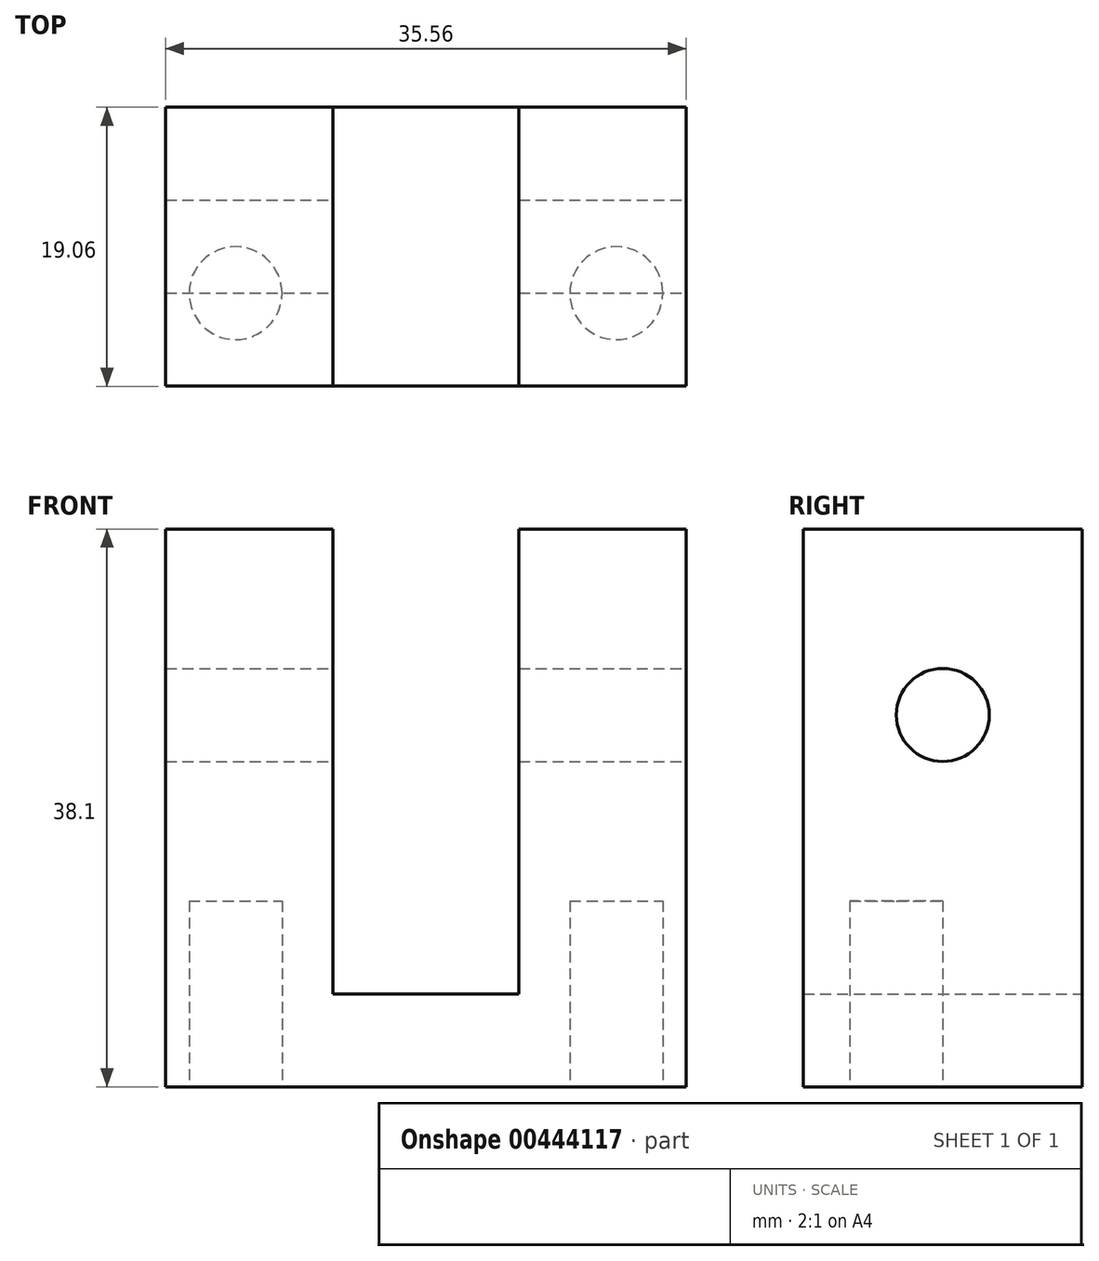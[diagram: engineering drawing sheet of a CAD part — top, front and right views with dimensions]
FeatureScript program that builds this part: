
annotation { "Feature Type Name" : "Feature", "Feature Type Description" : "" }
export const myFeature = defineFeature(function(context is Context, id is Id, definition is map)
    precondition{}
    {
        {
            var Q0;
            Q0=qCreatedBy(makeId("Front.planeOp"),FACE);
            var sketch = newSketch(context, id + "F0", { "sketchPlane" : qUnion([Q0])});
            skLineSegment(sketch, "E0", {"start": v(0, 0) * mm, "end": v(0, 38.1) * mm});
            skLineSegment(sketch, "E1", {"start": v(0, 38.1) * mm, "end": v(11.43, 38.1) * mm});
            skLineSegment(sketch, "E2", {"start": v(11.43, 38.1) * mm, "end": v(11.43, 6.35) * mm});
            skLineSegment(sketch, "E3", {"start": v(11.43, 6.35) * mm, "end": v(24.13, 6.35) * mm});
            skLineSegment(sketch, "E4", {"start": v(24.13, 6.35) * mm, "end": v(24.13, 38.1) * mm});
            skLineSegment(sketch, "E5", {"start": v(24.13, 38.1) * mm, "end": v(35.56, 38.1) * mm});
            skLineSegment(sketch, "E6", {"start": v(35.56, 38.1) * mm, "end": v(35.56, 0) * mm});
            skLineSegment(sketch, "E7", {"start": v(35.56, 0) * mm, "end": v(0, 0) * mm});
            skLineSegment(sketch, "E8", {"start": v(-7.8, 25.4) * mm, "end": v(70.8, 25.4) * mm, "construction": true});
            skSolve(sketch);
        }
        {
            var Q0;
            Q0 = qSketchRegion(id + "F0", true);
            extrude(context, id + "F1", {"entities" : qUnion([Q0]), "endBound" : BoundingType.SYMMETRIC, "depth" : 19.05 * mm});
        }
        {
            var Q0;
            Q0=makeQuery(id+"F1.opExtrude","SWEPT_FACE",FACE,{"disambiguationData":[OSD([sQuery(id+"F0.wireOp",EDGE,"E6")])]});
            var sketch = newSketch(context, id + "F2", { "sketchPlane" : qUnion([Q0])});
            skLineSegment(sketch, "E9", {"start": v(-10.35, 25.4) * mm, "end": v(27.89, 25.4) * mm, "construction": true});
            skCircle(sketch, "E10", {"center": v(0, 25.4) * mm, "radius": 3.18 * mm});
            skSolve(sketch);
        }
        {
            var Q0;
            Q0 = qSketchRegion(id + "F2", true);
            extrude(context, id + "F3", {"entities" : qUnion([Q0]), "operationType" : NewBodyOperationType.REMOVE, "endBound" : BoundingType.THROUGH_ALL, "oppositeDirection" : true, "depth" : 25.4 * mm});
        }
        {
            var Q0;
            Q0=makeQuery(id+"F1.opExtrude","SWEPT_FACE",FACE,{"disambiguationData":[OSD([sQuery(id+"F0.wireOp",EDGE,"E7")])]});
            var sketch = newSketch(context, id + "F4", { "sketchPlane" : qUnion([Q0])});
            skLineSegment(sketch, "E11", {"start": v(1.1, 3.17) * mm, "end": v(41.06, 3.18) * mm});
            skLineSegment(sketch, "E12", {"start": v(4.78, 12.63) * mm, "end": v(4.78, -13.15) * mm});
            skLineSegment(sketch, "E13", {"start": v(30.78, 11.2) * mm, "end": v(30.78, -17.61) * mm});
            skCircle(sketch, "E14", {"center": v(4.78, 3.17) * mm, "radius": 3.18 * mm});
            skCircle(sketch, "E15", {"center": v(30.78, 3.18) * mm, "radius": 3.18 * mm});
            skSolve(sketch);
        }
        {
            var Q0;
            Q0 = qSketchRegion(id + "F4", true);
            extrude(context, id + "F5", {"entities" : qUnion([Q0]), "operationType" : NewBodyOperationType.REMOVE, "oppositeDirection" : true, "depth" : 12.7 * mm});
        }
    });
